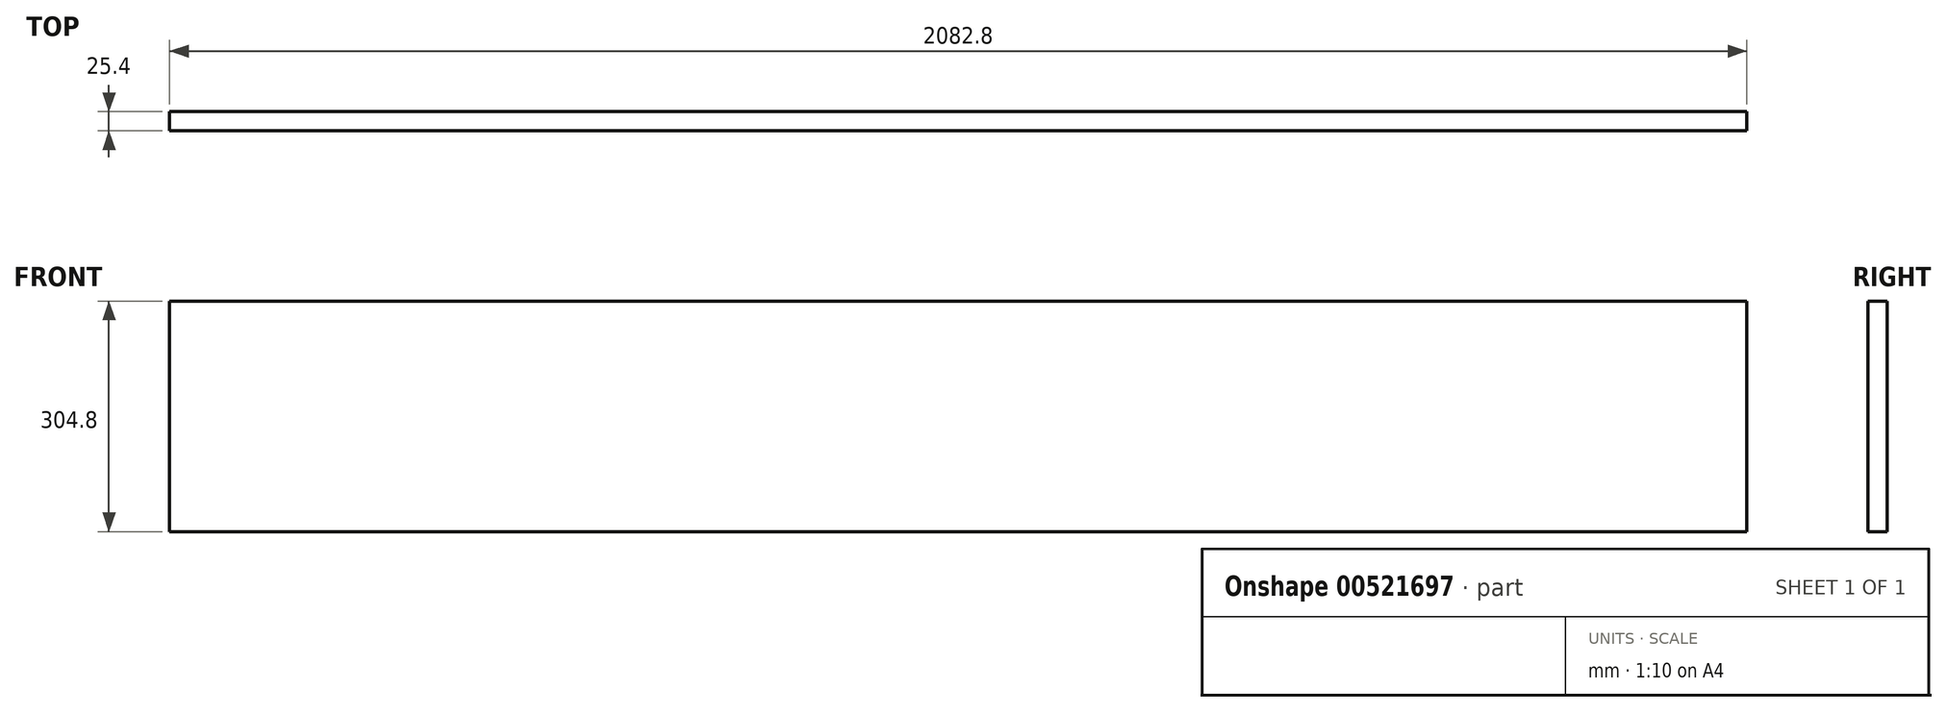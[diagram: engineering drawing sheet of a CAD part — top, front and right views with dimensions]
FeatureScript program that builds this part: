
annotation { "Feature Type Name" : "Feature", "Feature Type Description" : "" }
export const myFeature = defineFeature(function(context is Context, id is Id, definition is map)
    precondition{}
    {
        {
            var Q0;
            Q0=qCreatedBy(makeId("Front.planeOp"),FACE);
            var sketch = newSketch(context, id + "F0", { "sketchPlane" : qUnion([Q0])});
            skLineSegment(sketch, "E0.bottom", {"start": v(1041.4, 152.4) * mm, "end": v(-1041.4, 152.4) * mm});
            skLineSegment(sketch, "E0.top", {"start": v(1041.4, -152.4) * mm, "end": v(-1041.4, -152.4) * mm});
            skLineSegment(sketch, "E0.left", {"start": v(1041.4, 152.4) * mm, "end": v(1041.4, -152.4) * mm});
            skLineSegment(sketch, "E0.right", {"start": v(-1041.4, 152.4) * mm, "end": v(-1041.4, -152.4) * mm});
            skPoint(sketch, "E0.middle", {"position": v(0, 0) * mm});
            skSolve(sketch);
        }
        {
            var Q0;
            Q0 = qSketchRegion(id + "F0", true);
            extrude(context, id + "F1", {"entities" : qUnion([Q0]), "depth" : 25.4 * mm, "offsetDistance" : 25.4 * mm});
        }
    });
